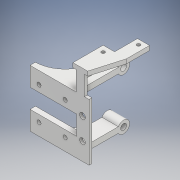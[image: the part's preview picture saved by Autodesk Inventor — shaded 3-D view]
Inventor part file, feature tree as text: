
AUTODESK INVENTOR PART (.ipt)
format: ipt  version: 2018.3 (Build 223284000, 284)  size: 1,079,296 bytes
history: native  units: mm
features: extrude x96, sketch x55, other x2, fillet x2
ambient origin geometry x8: Origin, YZ Plane, XZ Plane, XY Plane, X Axis, Y Axis, Z Axis, Center Point
bodies: Body1 (feature_tree)
feature tree (155):
  other  "Sólido1"
  extrude  "Extrusión1"  Depth=10.0mm TaperAngle=0.0deg
  extrude  "Extrusión2"  Depth=33.0mm TaperAngle=0.0deg
  extrude  "Extrusión3"  Depth=29.0mm TaperAngle=0.0deg
  extrude  "Extrusión4"  Depth=21.0mm
  extrude  "Extrusión5"  Depth=4.0mm TaperAngle=0.0deg
  extrude  "Extrusión6"  Depth=37.0mm TaperAngle=0.0deg
  extrude  "Extrusión7"  Depth=94.0mm TaperAngle=0.0deg
  extrude  "Extrusión8"  Depth=15.0mm
  extrude  "Extrusión9"  Depth=64.0mm TaperAngle=0.0deg
  extrude  "Extrusión10"  Depth=10.0mm
  extrude  "Extrusión11"  Depth=64.0mm TaperAngle=0.0deg
  extrude  "Extrusión13"  Depth=10.0mm
  extrude  "Extrusión14"  Depth=10.0mm
  extrude  "Extrusión15"  Depth=19.0mm TaperAngle=0.0deg
  extrude  "Extrusión17"  Depth=19.0mm TaperAngle=0.0deg
  extrude  "Extrusión18"  Depth=15.0mm TaperAngle=0.0deg
  extrude  "Extrusión19"  Depth=3.0mm
  extrude  "Extrusión20"  Depth=6.0mm TaperAngle=0.0deg
  extrude  "Extrusión21"  Depth=10.0mm TaperAngle=0.0deg
  extrude  "Extrusión22"  Depth=10.0mm TaperAngle=0.0deg
  extrude  "Extrusión23"  Depth=10.0mm TaperAngle=0.0deg
  extrude  "Extrusión27"  Depth=15.0mm
  extrude  "Extrusión28"  Depth=5.0mm
  extrude  "Extrusión29"  Depth=4.0mm TaperAngle=0.0deg
  extrude  "Extrusión30"  Depth=24.5mm TaperAngle=0.0deg
  extrude  "Extrusión31"  Depth=24.5mm TaperAngle=0.0deg
  extrude  "Extrusión32"  Depth=4.3mm
  extrude  "Extrusión33"  Depth=3.7mm
  extrude  "Extrusión35"  Depth=3.7mm
  extrude  "Extrusión36"  Depth=25.5mm TaperAngle=0.0deg
  extrude  "Extrusión38"  Depth=5.2mm
  extrude  "Extrusión39"  Depth=5.2mm
  extrude  "Extrusión40"  Depth=45.25mm TaperAngle=0.0deg
  extrude  "Extrusión41"  Depth=71.0mm TaperAngle=0.0deg
  extrude  "Extrusión42"  Depth=1.7mm TaperAngle=0.0deg
  extrude  "Extrusión43"  Depth=33.0mm
  extrude  "Extrusión44"  Depth=2.4mm TaperAngle=0.0deg
  extrude  "Extrusión45"  Depth=85.9mm TaperAngle=0.0deg
  extrude  "Extrusión46"  Depth=2.973mm
  extrude  "Extrusión47"  Depth=3.7mm
  extrude  "Extrusión48"  Depth=3.7mm
  extrude  "Extrusión49"  Depth=5.0mm TaperAngle=0.0deg
  extrude  "Extrusión50"  Depth=0.534mm
  extrude  "Extrusión53"  Depth=2.384mm TaperAngle=0.0deg
  extrude  "Extrusión54"  Depth=5.884mm TaperAngle=0.0deg
  extrude  "Extrusión55"  Depth=14.25mm TaperAngle=0.0deg
  extrude  "Extrusión56"  Depth=11.0mm TaperAngle=0.0deg
  extrude  "Extrusión57"  Depth=3.1mm
  sketch  "Boceto57"  dims[d115=23.0mm d116=0.0mm d117=4.0mm d118=0.0mm]
  extrude  "Extrusión58"  Depth=11.0mm
  extrude  "Extrusión59"  Depth=11.0mm TaperAngle=0.0deg
  extrude  "Extrusión60"  Depth=13.0mm TaperAngle=0.0deg
  extrude  "Extrusión61"  Depth=14.0mm TaperAngle=0.0deg
  extrude  "Extrusión62"  Depth=4.3mm
  extrude  "Extrusión63"  Depth=5.0mm TaperAngle=0.0deg
  extrude  "Extrusión64"  Depth=21.5mm TaperAngle=0.0deg
  extrude  "Extrusión65"  Depth=0.389mm
  extrude  "Extrusión66"  Depth=8.0mm TaperAngle=0.0deg
  extrude  "Extrusión67"  Depth=8.0mm TaperAngle=0.0deg
  extrude  "Extrusión68"  Depth=8.0mm TaperAngle=0.0deg
  extrude  "Extrusión69"  Depth=8.0mm TaperAngle=0.0deg
  extrude  "Extrusión74"  Depth=4.0mm TaperAngle=0.0deg
  extrude  "Extrusión75"  Depth=4.0mm TaperAngle=0.0deg
  extrude  "Extrusión76"  Depth=8.0mm TaperAngle=0.0deg
  extrude  "Extrusión77"  Depth=0.135mm
  extrude  "Extrusión78"  Depth=4.0mm TaperAngle=0.0deg
  extrude  "Extrusión79"  Depth=4.3mm TaperAngle=0.0deg
  extrude  "Extrusión80"  Depth=4.3mm TaperAngle=0.0deg
  extrude  "Extrusión81"  Depth=15.0mm TaperAngle=0.0deg
  extrude  "Extrusión82"  Depth=15.0mm TaperAngle=0.0deg
  extrude  "Extrusión83"  Depth=15.0mm TaperAngle=0.0deg
  extrude  "Extrusión84"  Depth=15.0mm TaperAngle=0.0deg
  extrude  "Extrusión85"  Depth=15.0mm TaperAngle=0.0deg
  extrude  "Extrusión86"  Depth=15.0mm TaperAngle=0.0deg
  extrude  "Extrusión87"  Depth=1.17mm TaperAngle=0.0deg
  extrude  "Extrusión88"  Depth=79.25mm TaperAngle=0.0deg
  extrude  "Extrusión89"  Depth=5.0mm TaperAngle=0.0deg
  extrude  "Extrusión90"  Depth=5.0mm TaperAngle=0.0deg
  extrude  "Extrusión91"  Depth=0.03mm TaperAngle=0.0deg
  extrude  "Extrusión92"  Depth=4.0mm TaperAngle=0.0deg
  extrude  "Extrusión93"  Depth=4.0mm TaperAngle=0.0deg
  extrude  "Extrusión94"  Depth=3.0mm
  extrude  "Extrusión95"  Depth=4.0mm TaperAngle=0.0deg
  extrude  "Extrusión96"  Depth=2.53mm TaperAngle=0.0deg
  extrude  "Extrusión97"  Depth=4.0mm TaperAngle=0.0deg
  extrude  "Extrusión98"  Depth=4.0mm TaperAngle=0.0deg
  extrude  "Extrusión99"  Depth=5.0mm TaperAngle=0.0deg
  extrude  "Extrusión100"  Depth=2.6mm TaperAngle=0.0deg
  extrude  "Extrusión101"  Depth=5.4mm
  extrude  "Extrusión102"  Depth=5.4mm
  extrude  "Extrusión103"  Depth=28.5mm TaperAngle=0.0deg
  extrude  "Extrusión109"  Depth=5.4mm
  extrude  "Extrusión110"  Depth=28.5mm TaperAngle=0.0deg
  extrude  "Extrusión112"  Depth=5.4mm
  extrude  "Extrusión113"  Depth=5.4mm
  extrude  "Extrusión114"  Depth=28.5mm TaperAngle=0.0deg
  extrude  "Extrusión115"  Depth=3.5mm TaperAngle=0.0deg
  fillet  "Empalme3"  Radius=2.5mm
  fillet  "Empalme4"  Radius=3.7mm
  sketch  "Boceto1"  dims[d0=18.0mm d1=0.0mm d2=10.0mm d3=0.0mm]
  sketch  "Boceto2"  dims[d6=3.0mm d7=33.0mm d8=0.0mm]
  sketch  "Boceto4"  dims[d9=35.0mm d10=29.0mm d11=0.0mm]
  sketch  "Boceto5"  dims[d12=2.0mm d13=21.0mm]
  sketch  "Boceto6"  dims[d14=20.0mm d15=4.0mm d16=0.0mm]
  sketch  "Boceto7"  dims[d17=8.0mm d18=0.0mm d19=37.0mm d20=0.0mm]
  sketch  "Boceto8"  dims[d21=2.0mm d22=94.0mm d23=0.0mm]
  sketch  "Boceto9"  dims[d30=5.0mm d31=15.0mm]
  sketch  "Boceto21"  dims[d32=15.0mm d33=64.0mm d34=0.0mm]
  sketch  "Boceto24"  dims[d35=64.0mm d36=0.0mm d38=10.0mm]
  sketch  "Boceto27"  dims[d40=15.0mm d41=64.0mm d42=0.0mm]
  sketch  "Boceto30"  dims[d48=46.25mm d49=10.0mm]
  sketch  "Boceto31"  dims[d50=23.0mm d51=0.0mm d52=10.0mm]
  sketch  "Boceto32"  dims[d53=19.0mm d54=0.0mm d58=19.0mm d59=0.0mm]
  sketch  "Boceto35"  dims[d68=19.0mm d69=0.0mm d70=19.0mm d71=0.0mm]
  sketch  "Boceto39"  dims[d73=19.0mm d74=0.0mm d76=15.0mm d77=0.0mm]
  sketch  "Boceto40"  dims[d78=4.0mm d79=0.0mm d80=3.0mm]
  sketch  "Boceto43"  dims[d81=6.0mm d82=0.0mm d87=6.0mm d88=0.0mm]
  sketch  "Boceto45"  dims[d89=4.0mm d96=10.0mm d97=0.0mm]
  sketch  "Boceto49"  dims[d101=10.0mm d102=0.0mm d104=10.0mm d105=0.0mm]
  sketch  "Boceto54"  dims[d106=2.0mm d107=10.0mm d108=0.0mm]
  sketch  "Boceto55"  dims[d110=11.0mm d111=15.0mm]
  sketch  "Boceto56"  dims[d112=10.0mm d113=0.0mm d114=5.0mm]
  sketch  "Boceto59"  dims[d124=24.5mm d125=0.0mm d132=24.5mm d133=0.0mm]
  sketch  "Boceto62"  dims[d141=24.5mm d142=0.0mm d145=24.5mm d146=0.0mm]
  sketch  "Boceto63"  dims[d147=10.0mm d148=0.0mm d149=4.3mm]
  sketch  "Boceto64"  dims[d150=4.3mm d151=3.7mm]
  sketch  "Boceto65"  dims[d152=3.7mm d153=3.7mm]
  sketch  "Boceto66"  dims[d154=3.7mm d155=25.5mm d156=0.0mm]
  sketch  "Boceto70"  dims[d157=5.2mm d158=5.2mm]
  sketch  "Boceto75"  dims[d159=25.5mm d160=0.0mm d161=5.2mm]
  sketch  "Boceto76"  dims[d162=5.2mm d163=45.25mm d164=0.0mm]
  sketch  "Boceto83"  dims[d165=2.6mm d166=71.0mm d167=0.0mm]
  sketch  "Boceto84"  dims[d168=10.005mm d169=1.7mm d170=0.0mm]
  sketch  "Boceto90"  dims[d171=33.0mm d172=33.0mm]
  sketch  "Boceto92"  dims[d173=38.28mm d174=4.0mm d175=0.0mm d176=0.0mm d178=2.4mm d179=0.0mm]
  sketch  "Boceto93"  dims[d180=6.15mm d181=0.0mm d184=85.9mm d185=0.0mm]
  sketch  "Boceto94"  dims[d186=2.973mm d187=2.973mm]
  sketch  "Boceto96"  dims[d188=5.0mm d189=0.0mm d205=3.7mm]
  sketch  "Boceto97"  dims[d209=3.7mm d210=3.7mm]
  sketch  "Boceto99"  dims[d211=3.7mm d212=5.0mm d213=0.0mm]
  sketch  "Boceto100"  dims[d214=5.0mm d215=0.0mm d216=0.534mm]
  sketch  "Boceto101"  dims[d217=5.0mm d218=0.0mm d219=2.384mm d220=0.0mm]
  sketch  "Boceto102"  dims[d221=17.6mm d222=5.884mm d223=0.0mm]
  sketch  "Boceto103"  dims[d224=3.25mm d225=14.25mm d226=0.0mm]
  sketch  "Boceto104"  dims[d227=11.0mm d228=0.0mm d229=11.0mm d230=0.0mm]
  sketch  "Boceto105"  dims[d233=3.1mm d234=3.1mm]
  sketch  "Boceto106"  dims[d235=11.0mm d236=0.0mm d237=11.0mm]
  sketch  "Boceto114"  dims[d238=11.0mm d239=11.0mm d240=0.0mm]
  sketch  "Boceto115"  dims[d241=11.0mm d242=0.0mm d243=13.0mm d244=0.0mm]
  sketch  "Boceto116"  dims[d245=23.0mm d246=0.0mm d247=14.0mm d248=0.0mm]
  sketch  "Boceto117"  dims[d249=15.0mm d250=0.0mm d251=4.3mm]
  sketch  "Boceto118"  dims[d252=8.0mm d253=0.0mm d254=5.0mm d255=0.0mm]
  sketch  "Boceto119"  dims[d268=1.0mm d269=21.5mm d270=0.0mm d271=0.389mm d272=8.0mm d273=0.0mm d276=8.0mm d277=0.0mm d279=8.0mm d280=0.0mm d282=8.0mm d283=0.0mm d285=4.0mm d286=0.0mm d288=4.0mm d289=0.0mm d291=8.0mm d292=0.0mm d293=0.135mm d294=4.0mm d295=0.0mm d296=4.3mm d297=0.0mm d299=4.3mm d300=0.0mm d303=15.0mm d304=0.0mm d306=15.0mm d307=0.0mm d309=15.0mm d310=0.0mm d311=15.0mm d312=0.0mm d314=15.0mm d315=0.0mm d316=15.0mm d317=0.0mm d318=1.17mm d319=0.0mm d320=79.25mm d321=0.0mm d334=5.0mm d335=0.0mm d336=5.0mm d337=0.0mm d338=0.03mm d339=0.0mm d340=4.0mm d341=0.0mm d342=4.0mm d343=0.0mm d344=3.0mm d345=4.0mm d346=0.0mm d347=2.53mm d348=0.0mm d349=4.0mm d350=0.0mm d352=4.0mm d353=0.0mm d354=5.0mm d355=0.0mm d356=2.6mm d357=0.0mm d381=5.4mm d382=5.4mm d383=28.5mm d384=0.0mm d385=5.4mm d386=28.5mm d387=0.0mm d388=5.4mm d389=5.4mm d392=28.5mm d393=0.0mm d394=3.5mm d395=0.0mm d396=2.5mm d397=3.7mm d398=2.5mm d399=3.7mm d400=2.5mm d401=3.7mm d402=2.5mm d403=3.7mm d404=9.75mm d405=0.0mm d406=5.0mm d407=0.0mm d410=27.5mm d411=27.5mm]
  other  "Saliente-Extruir7"
